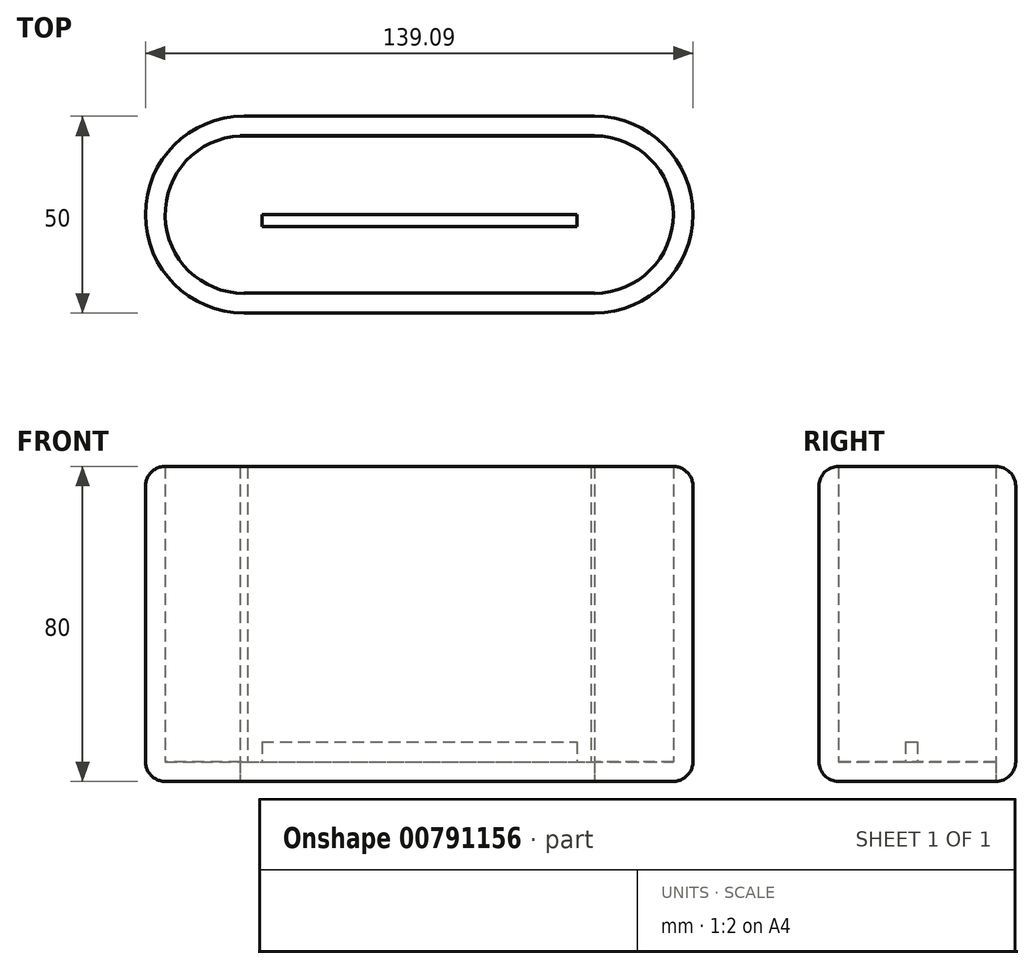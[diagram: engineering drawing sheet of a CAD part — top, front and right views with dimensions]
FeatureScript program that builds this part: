
annotation { "Feature Type Name" : "Feature", "Feature Type Description" : "" }
export const myFeature = defineFeature(function(context is Context, id is Id, definition is map)
    precondition{}
    {
        {
            var Q0;
            Q0=qCreatedBy(makeId("Top.planeOp"),FACE);
            var sketch = newSketch(context, id + "F0", { "sketchPlane" : qUnion([Q0])});
            skLineSegment(sketch, "E0.bottom", {"start": v(-44.45, 25) * mm, "end": v(44.64, 25) * mm});
            skLineSegment(sketch, "E0.top", {"start": v(-44.45, -25) * mm, "end": v(44.64, -25) * mm});
            skArc(sketch, "E1", {"start": v(-44.45, 25) * mm, "mid": v(-69.45, 0) * mm, "end": v(-44.45, -25) * mm});
            skArc(sketch, "E2", {"start": v(44.64, -25) * mm, "mid": v(69.64, 0) * mm, "end": v(44.64, 25) * mm});
            skLineSegment(sketch, "E3.bottom", {"start": v(-45.36, 20.02) * mm, "end": v(44.64, 20.02) * mm});
            skLineSegment(sketch, "E3.top", {"start": v(-45.36, -19.98) * mm, "end": v(44.64, -19.98) * mm});
            skLineSegment(sketch, "E3.left", {"start": v(-45.36, 20.02) * mm, "end": v(-45.36, 19.98) * mm});
            skLineSegment(sketch, "E3.right", {"start": v(44.64, 20.02) * mm, "end": v(44.64, 20) * mm});
            skArc(sketch, "E4", {"start": v(-45.36, 19.98) * mm, "mid": v(-64.43, -0.9) * mm, "end": v(-43.54, -19.98) * mm});
            skArc(sketch, "E5", {"start": v(43.73, -19.98) * mm, "mid": v(64.64, -0.45) * mm, "end": v(44.64, 20) * mm});
            skLineSegment(sketch, "E6.bottom", {"start": v(-39.8, -14.24) * mm, "end": v(40.2, -14.24) * mm});
            skLineSegment(sketch, "E6.top", {"start": v(-39.8, -1.24) * mm, "end": v(40.2, -1.24) * mm});
            skLineSegment(sketch, "E6.left", {"start": v(-39.8, -14.24) * mm, "end": v(-39.8, -1.24) * mm});
            skLineSegment(sketch, "E6.right", {"start": v(40.2, -14.24) * mm, "end": v(40.2, -1.24) * mm});
            skSolve(sketch);
        }
        {
            var Q0;
            Q0=qCreatedBy(makeId("Top.planeOp"),FACE);
            var sketch = newSketch(context, id + "F1", { "sketchPlane" : qUnion([Q0])});
            skLineSegment(sketch, "E7.bottom", {"start": v(-44.9, 20) * mm, "end": v(45.1, 20) * mm});
            skLineSegment(sketch, "E7.top", {"start": v(-44.9, -20) * mm, "end": v(45.1, -20) * mm});
            skArc(sketch, "E8", {"start": v(-44.9, 20) * mm, "mid": v(-64.9, 0) * mm, "end": v(-44.9, -20) * mm});
            skPoint(sketch, "E8.centerSnap0", {"position": v(-44.9, 0) * mm});
            skArc(sketch, "E9", {"start": v(45.1, -20) * mm, "mid": v(65.1, 0) * mm, "end": v(45.1, 20) * mm});
            skLineSegment(sketch, "E10.bottom", {"start": v(-39.87, -20) * mm, "end": v(40.13, -20) * mm});
            skSolve(sketch);
        }
        {
            var Q0;
            Q0=makeQuery(id+"F0.imprint","IMPRINT",FACE,{"disambiguationData":[TD([[makeQuery(id+"F0.imprint","IMPRINT",EDGE,{"derivedFrom":sQuery(id+"F0.wireOp",EDGE,"E0.bottom")}),-1.0]])]});
            extrude(context, id + "F2", {"entities" : qUnion([Q0]), "depth" : 80 * mm, "offsetDistance" : 25 * mm});
        }
        {
            var Q0;
            Q0 = qSketchRegion(id + "F1", true);
            extrude(context, id + "F3", {"entities" : qUnion([Q0]), "operationType" : NewBodyOperationType.ADD, "depth" : 5 * mm, "offsetDistance" : 25 * mm});
        }
        {
            var Q0;
            Q0=makeQuery(id+"F3.opExtrude","CAP_FACE",FACE,{"disambiguationData":[OSD([sQuery(id+"F1.wireOp",EDGE,"E7.bottom"),sQuery(id+"F1.wireOp",EDGE,"E7.top"),sQuery(id+"F1.wireOp",EDGE,"E8"),sQuery(id+"F1.wireOp",EDGE,"E9"),sQuery(id+"F1.wireOp",EDGE,"E10.bottom")])],"isStart":false});
            var sketch = newSketch(context, id + "F4", { "sketchPlane" : qUnion([Q0])});
            skLineSegment(sketch, "E11.bottom", {"start": v(-39.87, -3) * mm, "end": v(40.13, -3) * mm});
            skLineSegment(sketch, "E11.top", {"start": v(-39.87, 0) * mm, "end": v(40.13, 0) * mm});
            skLineSegment(sketch, "E11.left", {"start": v(-39.87, -3) * mm, "end": v(-39.87, 0) * mm});
            skLineSegment(sketch, "E11.right", {"start": v(40.13, -3) * mm, "end": v(40.13, 0) * mm});
            skSolve(sketch);
        }
        {
            var Q0;
            Q0 = qSketchRegion(id + "F4", true);
            extrude(context, id + "F5", {"entities" : qUnion([Q0]), "operationType" : NewBodyOperationType.ADD, "depth" : 5 * mm, "offsetDistance" : 25 * mm});
        }
        {
            var Q0;
            Q0=makeQuery(id+"F2.opExtrude","CAP_EDGE",EDGE,{"disambiguationData":[OSD([sQuery(id+"F0.wireOp",EDGE,"E0.top")])],"isStart":false});
            fillet(context, id + "F6", {"entities" : qUnion([Q0]), "radius" : 5 * mm, "tangentPropagation" : true, "allowEdgeOverflow" : false});
        }
        {
            var Q0;
            Q0=makeQuery(id+"F2.opExtrude","CAP_EDGE",EDGE,{"disambiguationData":[OSD([sQuery(id+"F0.wireOp",EDGE,"E1")])],"isStart":true});
            var Q1;
            Q1=makeQuery(id+"F2.opExtrude","SWEPT_FACE",FACE,{"disambiguationData":[OSD([sQuery(id+"F0.wireOp",EDGE,"E0.top")])]});
            fillet(context, id + "F7", {"entities" : qUnion([Q0, Q1]), "radius" : 5 * mm, "tangentPropagation" : true, "allowEdgeOverflow" : false});
        }
    });
